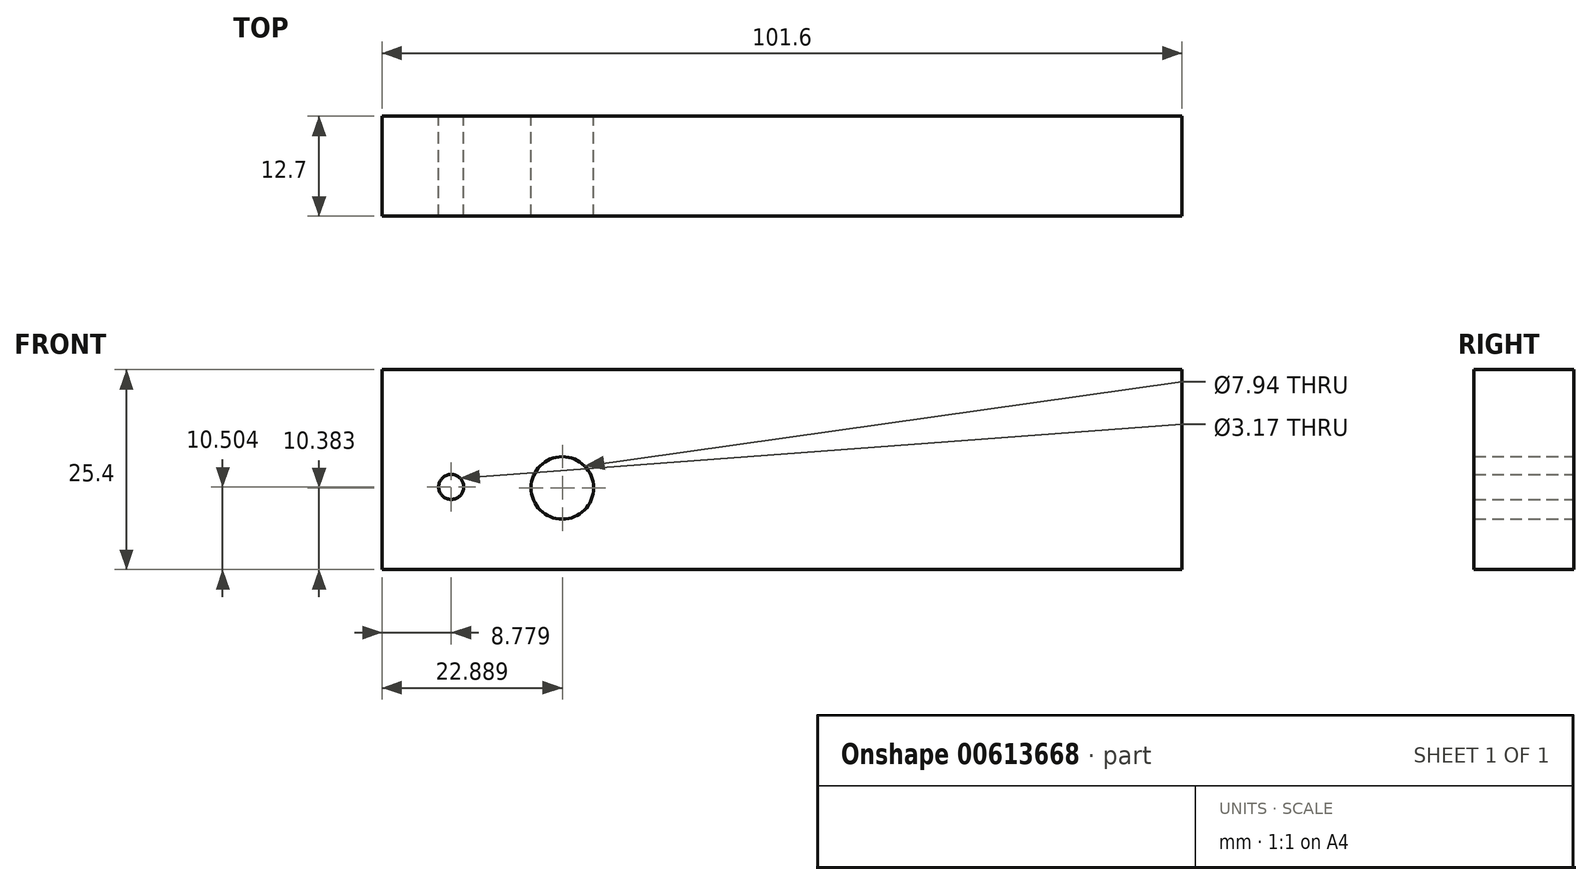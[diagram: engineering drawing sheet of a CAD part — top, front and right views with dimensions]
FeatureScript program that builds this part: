
annotation { "Feature Type Name" : "Feature", "Feature Type Description" : "" }
export const myFeature = defineFeature(function(context is Context, id is Id, definition is map)
    precondition{}
    {
        {
            var Q0;
            Q0=qCreatedBy(makeId("Front.planeOp"),FACE);
            var sketch = newSketch(context, id + "F0", { "sketchPlane" : qUnion([Q0])});
            skLineSegment(sketch, "E0.bottom", {"start": v(-26.7, 38) * mm, "end": v(74.9, 38) * mm});
            skLineSegment(sketch, "E0.top", {"start": v(-26.7, 12.6) * mm, "end": v(74.9, 12.6) * mm});
            skLineSegment(sketch, "E0.left", {"start": v(-26.7, 38) * mm, "end": v(-26.7, 12.6) * mm});
            skLineSegment(sketch, "E0.right", {"start": v(74.9, 38) * mm, "end": v(74.9, 12.6) * mm});
            skCircle(sketch, "E1", {"center": v(-3.81, 22.98) * mm, "radius": 3.97 * mm});
            skPoint(sketch, "E1.first.point", {"position": v(-6, 26.29) * mm});
            skPoint(sketch, "E1.second.point", {"position": v(0, 21.87) * mm});
            skPoint(sketch, "E1.third.point", {"position": v(0, 24.1) * mm});
            skCircle(sketch, "E2", {"center": v(-17.92, 23.1) * mm, "radius": 1.59 * mm});
            skSolve(sketch);
        }
        {
            var Q0;
            Q0 = qSketchRegion(id + "F0", true);
            extrude(context, id + "F1", {"entities" : qUnion([Q0]), "depth" : 12.7 * mm, "offsetDistance" : 25.4 * mm});
        }
    });
